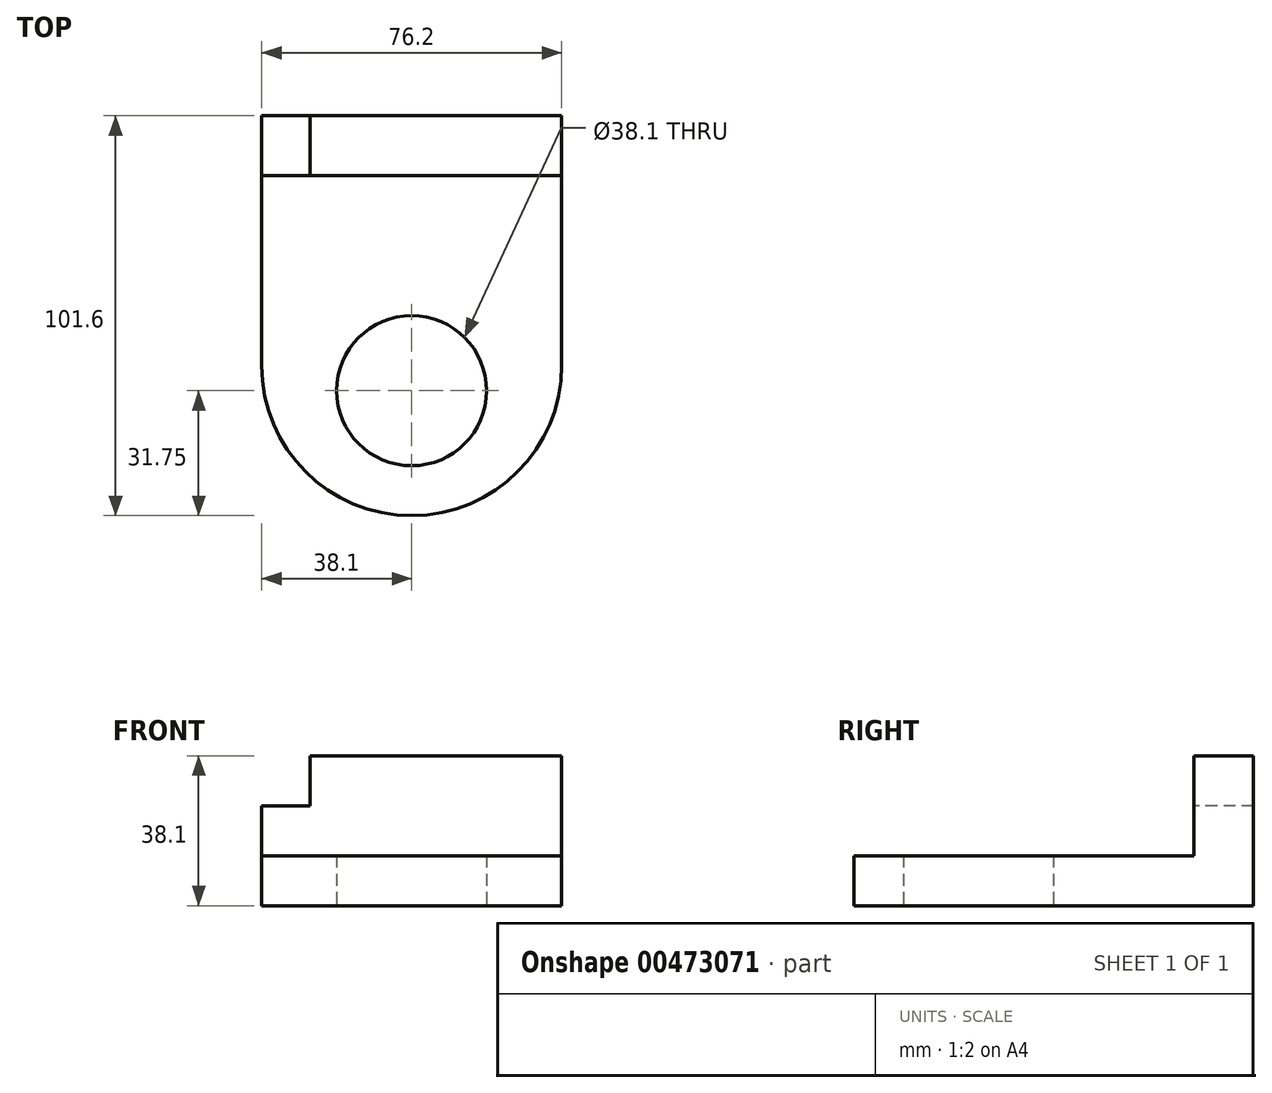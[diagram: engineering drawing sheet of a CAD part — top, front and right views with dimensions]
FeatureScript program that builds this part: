
annotation { "Feature Type Name" : "Feature", "Feature Type Description" : "" }
export const myFeature = defineFeature(function(context is Context, id is Id, definition is map)
    precondition{}
    {
        {
            var Q0;
            Q0=qCreatedBy(makeId("Top.planeOp"),FACE);
            var sketch = newSketch(context, id + "F0", { "sketchPlane" : qUnion([Q0])});
            skLineSegment(sketch, "E0.bottom", {"start": v(-38.1, 50.8) * mm, "end": v(38.1, 50.8) * mm});
            skLineSegment(sketch, "E0.top", {"start": v(-38.1, -50.8) * mm, "end": v(38.1, -50.8) * mm});
            skLineSegment(sketch, "E0.left", {"start": v(-38.1, 50.8) * mm, "end": v(-38.1, -50.8) * mm});
            skLineSegment(sketch, "E0.right", {"start": v(38.1, 50.8) * mm, "end": v(38.1, -50.8) * mm});
            skPoint(sketch, "E0.middle", {"position": v(0, 0) * mm});
            skSolve(sketch);
        }
        {
            var Q0;
            Q0 = qSketchRegion(id + "F0", true);
            extrude(context, id + "F1", {"entities" : qUnion([Q0]), "depth" : 12.7 * mm});
        }
        {
            var Q0;
            Q0=qCreatedBy(makeId("Front.planeOp"),FACE);
            var sketch = newSketch(context, id + "F2", { "sketchPlane" : qUnion([Q0])});
            skLineSegment(sketch, "E1.bottom", {"start": v(-38.1, 25.4) * mm, "end": v(38.1, 25.4) * mm});
            skLineSegment(sketch, "E1.top", {"start": v(-38.1, 12.7) * mm, "end": v(38.1, 12.7) * mm});
            skLineSegment(sketch, "E1.left", {"start": v(-38.1, 25.4) * mm, "end": v(-38.1, 12.7) * mm});
            skLineSegment(sketch, "E1.right", {"start": v(38.1, 25.4) * mm, "end": v(38.1, 12.7) * mm});
            skLineSegment(sketch, "E2.bottom", {"start": v(-25.83, 25.4) * mm, "end": v(38.1, 25.4) * mm});
            skLineSegment(sketch, "E2.top", {"start": v(-25.83, 38.1) * mm, "end": v(38.1, 38.1) * mm});
            skLineSegment(sketch, "E2.left", {"start": v(-25.83, 25.4) * mm, "end": v(-25.83, 38.1) * mm});
            skLineSegment(sketch, "E2.right", {"start": v(38.1, 25.4) * mm, "end": v(38.1, 38.1) * mm});
            skSolve(sketch);
        }
        {
            var Q0;
            Q0 = qSketchRegion(id + "F2", true);
            var Q1;
            Q1=makeQuery(id+"F1.opExtrude","SWEPT_FACE",FACE,{"disambiguationData":[OSD([sQuery(id+"F0.wireOp",EDGE,"E0.bottom")])]});
            extrude(context, id + "F3", {"entities" : qUnion([Q0]), "operationType" : NewBodyOperationType.ADD, "oppositeDirection" : true, "endBoundEntityFace" : qUnion([Q1]), "depth" : 50.8 * mm});
        }
        {
            var Q0;
            Q0=makeQuery(id+"F3.opExtrude","CAP_FACE",FACE,{"disambiguationData":[OSD([sQuery(id+"F2.wireOp",EDGE,"E1.bottom"),sQuery(id+"F2.wireOp",EDGE,"E1.top"),sQuery(id+"F2.wireOp",EDGE,"E1.left"),sQuery(id+"F2.wireOp",EDGE,"E1.right")])],"isStart":true});
            extrude(context, id + "F4", {"entities" : qUnion([Q0]), "operationType" : NewBodyOperationType.REMOVE, "oppositeDirection" : true, "depth" : 35.56 * mm});
        }
        {
            var Q0;
            Q0=qCreatedBy(makeId("Top.planeOp"),FACE);
            var sketch = newSketch(context, id + "F5", { "sketchPlane" : qUnion([Q0])});
            skCircle(sketch, "E3", {"center": v(0, -19.05) * mm, "radius": 19.05 * mm});
            skSolve(sketch);
        }
        {
            var Q0;
            Q0 = qSketchRegion(id + "F5", true);
            extrude(context, id + "F6", {"entities" : qUnion([Q0]), "operationType" : NewBodyOperationType.REMOVE, "endBound" : BoundingType.THROUGH_ALL, "depth" : 25.4 * mm});
        }
        {
            var Q0;
            Q0=makeQuery(id+"F1.opExtrude","SWEPT_EDGE",EDGE,{"disambiguationData":[OSD([sQuery(id+"F0.wireOp",EDGE,"E0.top"),sQuery(id+"F0.wireOp",EDGE,"E0.left")])]});
            var Q1;
            Q1=makeQuery(id+"F1.opExtrude","SWEPT_EDGE",EDGE,{"disambiguationData":[OSD([sQuery(id+"F0.wireOp",EDGE,"E0.top"),sQuery(id+"F0.wireOp",EDGE,"E0.right")])]});
            fillet(context, id + "F7", {"entities" : qUnion([Q0, Q1]), "radius" : 38.1 * mm, "tangentPropagation" : true, "allowEdgeOverflow" : false});
        }
    });
